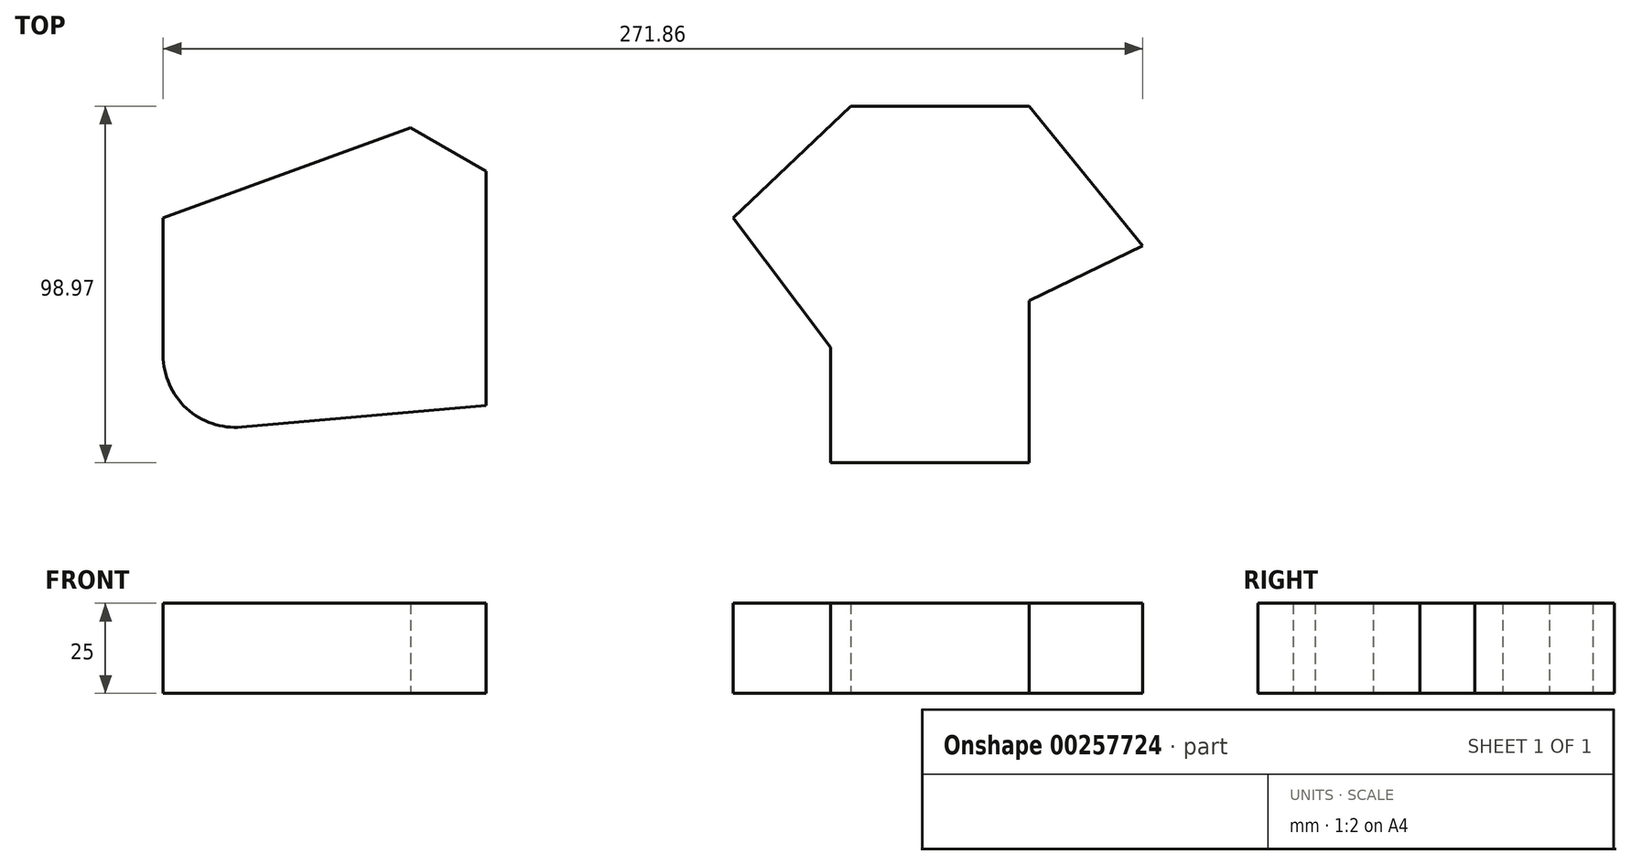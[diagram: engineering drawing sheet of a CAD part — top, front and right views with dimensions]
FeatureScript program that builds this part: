
annotation { "Feature Type Name" : "Feature", "Feature Type Description" : "" }
export const myFeature = defineFeature(function(context is Context, id is Id, definition is map)
    precondition{}
    {
        {
            var Q0;
            Q0=qCreatedBy(makeId("Top.planeOp"),FACE);
            var sketch = newSketch(context, id + "F0", { "sketchPlane" : qUnion([Q0])});
            skLineSegment(sketch, "E0", {"start": v(-11.1, -68) * mm, "end": v(43.9, -68) * mm});
            skLineSegment(sketch, "E1", {"start": v(-11.1, -68) * mm, "end": v(-11.1, -35.95) * mm});
            skLineSegment(sketch, "E2", {"start": v(-11.1, -35.95) * mm, "end": v(-38.15, 0) * mm});
            skLineSegment(sketch, "E3", {"start": v(-38.15, 0) * mm, "end": v(-5.5, 30.97) * mm});
            skLineSegment(sketch, "E4", {"start": v(-5.5, 30.97) * mm, "end": v(43.9, 30.97) * mm});
            skLineSegment(sketch, "E5", {"start": v(43.9, 30.97) * mm, "end": v(75.45, -7.82) * mm});
            skLineSegment(sketch, "E6", {"start": v(75.45, -7.82) * mm, "end": v(43.9, -23) * mm});
            skLineSegment(sketch, "E7", {"start": v(43.9, -23) * mm, "end": v(43.9, -68) * mm});
            skSolve(sketch);
        }
        {
            var Q0;
            Q0=qCreatedBy(makeId("Top.planeOp"),FACE);
            var sketch = newSketch(context, id + "F1", { "sketchPlane" : qUnion([Q0])});
            skLineSegment(sketch, "E8", {"start": v(-196.4, 0) * mm, "end": v(-196.4, -38.16) * mm});
            skLineSegment(sketch, "E9", {"start": v(-106.76, 12.9) * mm, "end": v(-106.76, -52.1) * mm});
            skLineSegment(sketch, "E10", {"start": v(-106.76, -52.1) * mm, "end": v(-174.65, -58.08) * mm});
            skPoint(sketch, "E11.visualSharp", {"position": v(-196.4, -60) * mm});
            skLineSegment(sketch, "E12", {"start": v(-174.65, -58.08) * mm, "end": v(-174.65, -58.08) * mm});
            skArc(sketch, "E13.filletArc", {"start": v(-196.4, -38.16) * mm, "mid": v(-189.92, -52.91) * mm, "end": v(-174.65, -58.08) * mm});
            skLineSegment(sketch, "E14", {"start": v(-196.4, 0) * mm, "end": v(-127.72, 25) * mm});
            skLineSegment(sketch, "E15", {"start": v(-127.72, 25) * mm, "end": v(-106.76, 12.9) * mm});
            skLineSegment(sketch, "E16", {"start": v(-106.76, 12.9) * mm, "end": v(-127.72, 12.9) * mm});
            skLineSegment(sketch, "E17", {"start": v(-161.87, 0) * mm, "end": v(-196.4, 0) * mm});
            skSolve(sketch);
        }
        {
            var Q0;
            Q0=makeQuery(id+"F1.imprint","IMPRINT",FACE,{"disambiguationData":[TD([[makeQuery(id+"F1.imprint","IMPRINT",EDGE,{"derivedFrom":sQuery(id+"F1.wireOp",EDGE,"E8")}),1.0]])]});
            extrude(context, id + "F2", {"entities" : qUnion([Q0]), "depth" : 25 * mm});
        }
        {
            var Q0;
            Q0=makeQuery(id+"F0.imprint","IMPRINT",FACE,{"disambiguationData":[TD([[makeQuery(id+"F0.imprint","IMPRINT",EDGE,{"derivedFrom":sQuery(id+"F0.wireOp",EDGE,"E0")}),1.0]])]});
            extrude(context, id + "F3", {"entities" : qUnion([Q0]), "depth" : 25 * mm});
        }
    });
